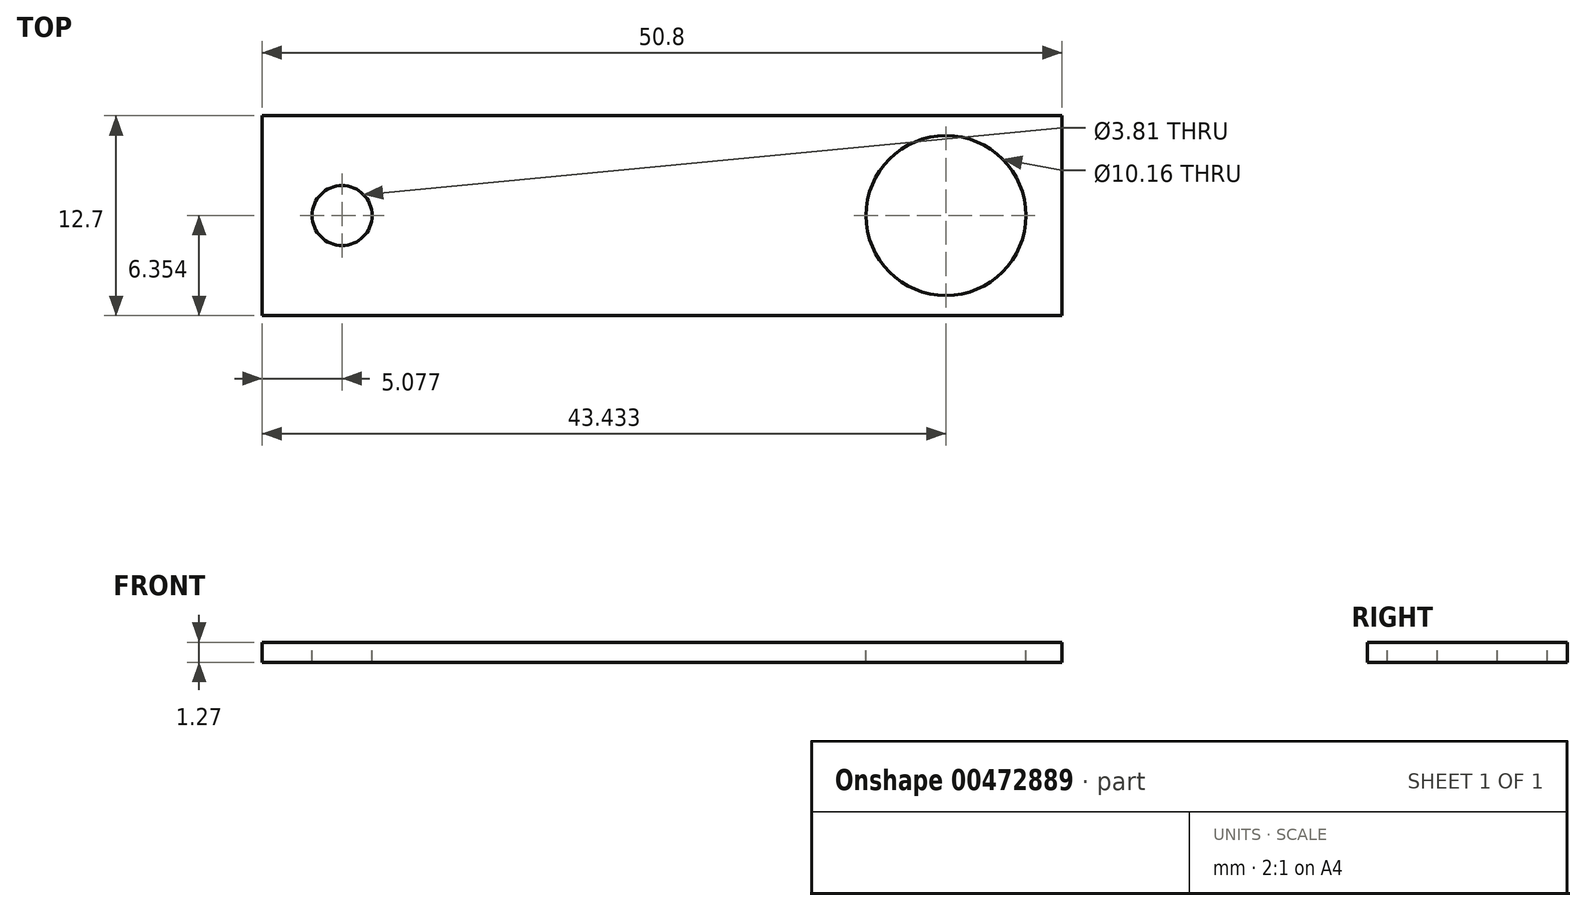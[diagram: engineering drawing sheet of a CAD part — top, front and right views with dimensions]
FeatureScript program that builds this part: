
annotation { "Feature Type Name" : "Feature", "Feature Type Description" : "" }
export const myFeature = defineFeature(function(context is Context, id is Id, definition is map)
    precondition{}
    {
        {
            var Q0;
            Q0=qCreatedBy(makeId("Top.planeOp"),FACE);
            var sketch = newSketch(context, id + "F0", { "sketchPlane" : qUnion([Q0])});
            skLineSegment(sketch, "E0.bottom", {"start": v(18.06, -27.4) * mm, "end": v(68.86, -27.4) * mm});
            skLineSegment(sketch, "E0.top", {"start": v(18.06, -14.7) * mm, "end": v(68.86, -14.7) * mm});
            skLineSegment(sketch, "E0.left", {"start": v(18.06, -27.4) * mm, "end": v(18.06, -14.7) * mm});
            skLineSegment(sketch, "E0.right", {"start": v(68.86, -27.4) * mm, "end": v(68.86, -14.7) * mm});
            skSolve(sketch);
        }
        {
            var Q0;
            Q0=makeQuery(id+"F0.imprint","IMPRINT",FACE,{"disambiguationData":[TD([[makeQuery(id+"F0.imprint","IMPRINT",EDGE,{"derivedFrom":sQuery(id+"F0.wireOp",EDGE,"E0.bottom")}),1.0]])]});
            extrude(context, id + "F1", {"entities" : qUnion([Q0]), "depth" : 1.27 * mm});
        }
        {
            var Q0;
            Q0=makeQuery(id+"F1.opExtrude","CAP_FACE",FACE,{"disambiguationData":[OSD([sQuery(id+"F0.wireOp",EDGE,"E0.bottom"),sQuery(id+"F0.wireOp",EDGE,"E0.top"),sQuery(id+"F0.wireOp",EDGE,"E0.left"),sQuery(id+"F0.wireOp",EDGE,"E0.right")])],"isStart":false});
            var sketch = newSketch(context, id + "F2", { "sketchPlane" : qUnion([Q0])});
            skCircle(sketch, "E1", {"center": v(23.14, -21.06) * mm, "radius": 1.9 * mm});
            skSolve(sketch);
        }
        {
            var Q0;
            Q0=makeQuery(id+"F2.imprint","IMPRINT",FACE,{"disambiguationData":[TD([[makeQuery(id+"F2.imprint","IMPRINT",EDGE,{"derivedFrom":sQuery(id+"F2.wireOp",EDGE,"E1")}),1.0]])]});
            extrude(context, id + "F3", {"entities" : qUnion([Q0]), "operationType" : NewBodyOperationType.REMOVE, "oppositeDirection" : true, "depth" : 25.4 * mm});
        }
        {
            var Q0;
            Q0=makeQuery(id+"F1.opExtrude","CAP_FACE",FACE,{"disambiguationData":[OSD([sQuery(id+"F0.wireOp",EDGE,"E0.bottom"),sQuery(id+"F0.wireOp",EDGE,"E0.top"),sQuery(id+"F0.wireOp",EDGE,"E0.left"),sQuery(id+"F0.wireOp",EDGE,"E0.right")])],"isStart":false});
            var sketch = newSketch(context, id + "F4", { "sketchPlane" : qUnion([Q0])});
            skCircle(sketch, "E2", {"center": v(61.5, -21.06) * mm, "radius": 5.08 * mm});
            skPoint(sketch, "E2.centerSnap0", {"position": v(68.86, -21.06) * mm});
            skSolve(sketch);
        }
        {
            var Q0;
            Q0=makeQuery(id+"F4.imprint","IMPRINT",FACE,{"disambiguationData":[TD([[makeQuery(id+"F4.imprint","IMPRINT",EDGE,{"derivedFrom":sQuery(id+"F4.wireOp",EDGE,"E2")}),1.0]])]});
            extrude(context, id + "F5", {"entities" : qUnion([Q0]), "operationType" : NewBodyOperationType.REMOVE, "oppositeDirection" : true, "depth" : 25.4 * mm});
        }
    });
